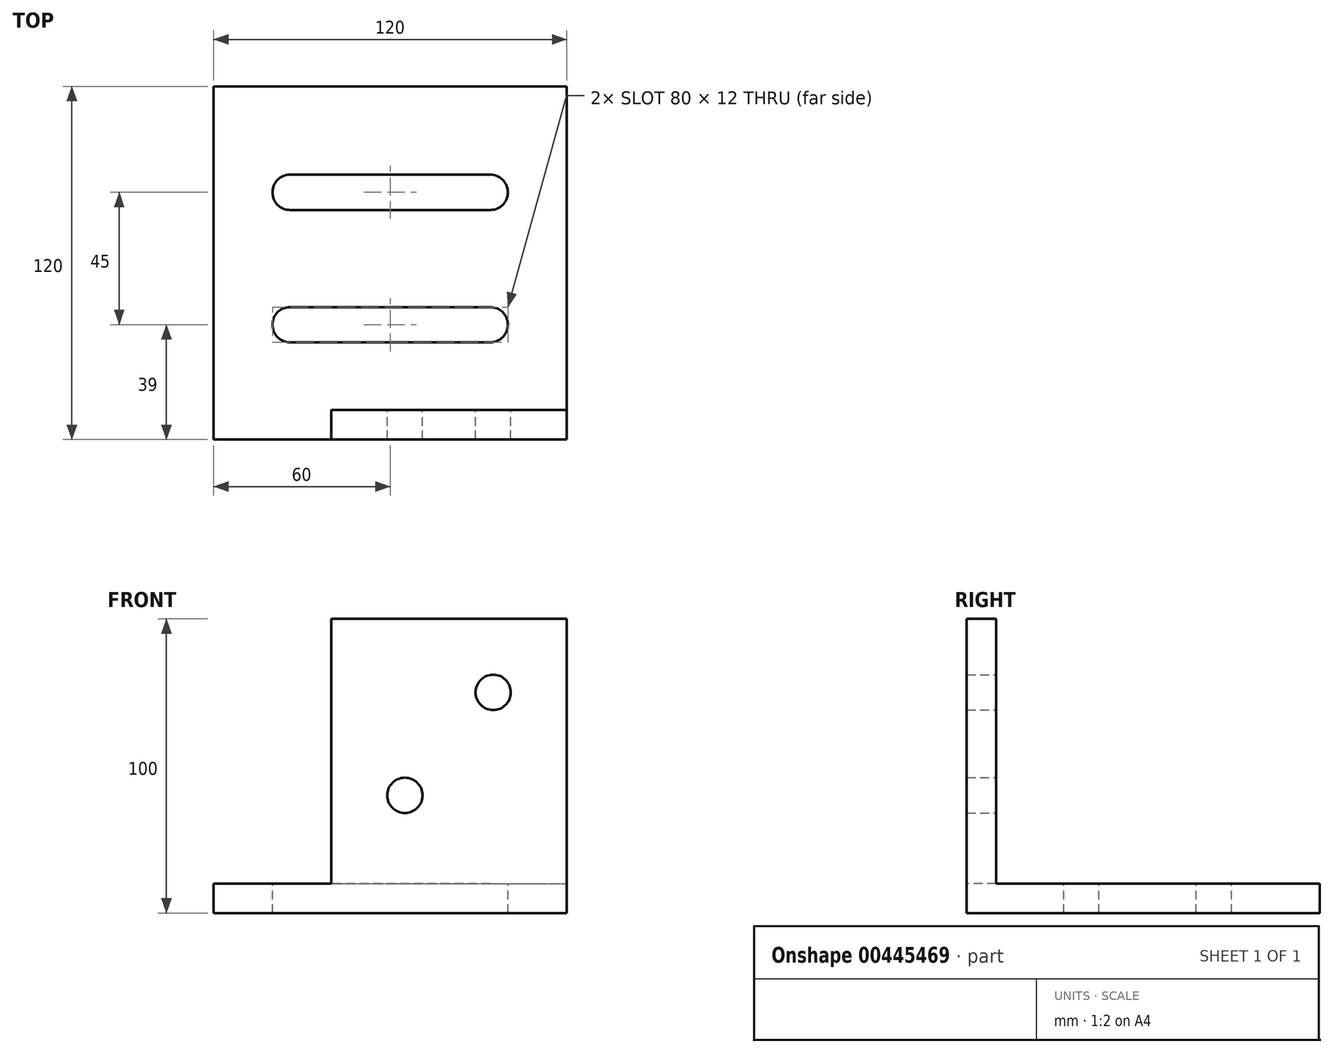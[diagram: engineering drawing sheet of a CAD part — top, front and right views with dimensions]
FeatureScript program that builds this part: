
annotation { "Feature Type Name" : "Feature", "Feature Type Description" : "" }
export const myFeature = defineFeature(function(context is Context, id is Id, definition is map)
    precondition{}
    {
        {
            var Q0;
            Q0=qCreatedBy(makeId("Front.planeOp"),FACE);
            var sketch = newSketch(context, id + "F0", { "sketchPlane" : qUnion([Q0])});
            skLineSegment(sketch, "E0.bottom", {"start": v(40, -50) * mm, "end": v(-40, -50) * mm});
            skLineSegment(sketch, "E0.top", {"start": v(40, 50) * mm, "end": v(-40, 50) * mm});
            skLineSegment(sketch, "E0.left", {"start": v(40, -50) * mm, "end": v(40, 50) * mm});
            skLineSegment(sketch, "E0.right", {"start": v(-40, -50) * mm, "end": v(-40, 50) * mm});
            skPoint(sketch, "E0.middle", {"position": v(0, 0) * mm});
            skSolve(sketch);
        }
        {
            var Q0;
            Q0 = qSketchRegion(id + "F0", true);
            extrude(context, id + "F1", {"entities" : qUnion([Q0]), "endBound" : BoundingType.SYMMETRIC, "depth" : 10 * mm, "offsetDistance" : 25 * mm});
        }
        {
            var Q0;
            Q0=makeQuery(id+"F1.opExtrude","CAP_FACE",FACE,{"disambiguationData":[OSD([sQuery(id+"F0.wireOp",EDGE,"E0.bottom"),sQuery(id+"F0.wireOp",EDGE,"E0.top"),sQuery(id+"F0.wireOp",EDGE,"E0.left"),sQuery(id+"F0.wireOp",EDGE,"E0.right")])],"isStart":false});
            var sketch = newSketch(context, id + "F2", { "sketchPlane" : qUnion([Q0])});
            skLineSegment(sketch, "E1.bottom", {"start": v(-80, -50) * mm, "end": v(40, -50) * mm});
            skLineSegment(sketch, "E1.top", {"start": v(-80, -40) * mm, "end": v(40, -40) * mm});
            skLineSegment(sketch, "E1.left", {"start": v(-80, -50) * mm, "end": v(-80, -40) * mm});
            skLineSegment(sketch, "E1.right", {"start": v(40, -50) * mm, "end": v(40, -40) * mm});
            skSolve(sketch);
        }
        {
            var Q0;
            Q0 = qSketchRegion(id + "F2", true);
            extrude(context, id + "F3", {"entities" : qUnion([Q0]), "operationType" : NewBodyOperationType.ADD, "oppositeDirection" : true, "depth" : 120 * mm, "offsetDistance" : 25 * mm});
        }
        {
            var Q0;
            Q0=makeQuery(id+"F3.opExtrude","SWEPT_FACE",FACE,{"disambiguationData":[OSD([sQuery(id+"F2.wireOp",EDGE,"E1.top")])]});
            var sketch = newSketch(context, id + "F4", { "sketchPlane" : qUnion([Q0])});
            skLineSegment(sketch, "E2.bottom", {"start": v(14, 85) * mm, "end": v(-54, 85) * mm});
            skLineSegment(sketch, "E2.top", {"start": v(14, 73) * mm, "end": v(-54, 73) * mm});
            skLineSegment(sketch, "E2.left", {"start": v(20, 79) * mm, "end": v(20, 79) * mm});
            skLineSegment(sketch, "E2.right", {"start": v(-60, 79) * mm, "end": v(-60, 79) * mm});
            skPoint(sketch, "E3.visualSharp", {"position": v(20, 85) * mm});
            skArc(sketch, "E3.filletArc", {"start": v(20, 79) * mm, "mid": v(18.24, 83.24) * mm, "end": v(14, 85) * mm});
            skPoint(sketch, "E4.visualSharp", {"position": v(20, 73) * mm});
            skArc(sketch, "E4.filletArc", {"start": v(14, 73) * mm, "mid": v(18.24, 74.76) * mm, "end": v(20, 79) * mm});
            skPoint(sketch, "E5.visualSharp", {"position": v(-60, 73) * mm});
            skArc(sketch, "E5.filletArc", {"start": v(-60, 79) * mm, "mid": v(-58.24, 74.76) * mm, "end": v(-54, 73) * mm});
            skPoint(sketch, "E6.visualSharp", {"position": v(-60, 85) * mm});
            skArc(sketch, "E6.filletArc", {"start": v(-54, 85) * mm, "mid": v(-58.24, 83.24) * mm, "end": v(-60, 79) * mm});
            skPoint(sketch, "E7.0.1.0", {"position": v(-60, 40) * mm});
            skPoint(sketch, "E7.0.1.1", {"position": v(-60, 28) * mm});
            skPoint(sketch, "E7.0.1.2", {"position": v(20, 40) * mm});
            skLineSegment(sketch, "E7.0.1.3", {"start": v(14, 28) * mm, "end": v(-54, 28) * mm});
            skPoint(sketch, "E7.0.1.4", {"position": v(20, 28) * mm});
            skLineSegment(sketch, "E7.0.1.5", {"start": v(14, 40) * mm, "end": v(-54, 40) * mm});
            skArc(sketch, "E7.0.1.6", {"start": v(20, 34) * mm, "mid": v(18.24, 38.24) * mm, "end": v(14, 40) * mm});
            skArc(sketch, "E7.0.1.7", {"start": v(-54, 40) * mm, "mid": v(-58.24, 38.24) * mm, "end": v(-60, 34) * mm});
            skArc(sketch, "E7.0.1.8", {"start": v(-60, 34) * mm, "mid": v(-58.24, 29.76) * mm, "end": v(-54, 28) * mm});
            skArc(sketch, "E7.0.1.9", {"start": v(14, 28) * mm, "mid": v(18.24, 29.76) * mm, "end": v(20, 34) * mm});
            skLineSegment(sketch, "E7.direction1", {"start": v(-60, 73) * mm, "end": v(-35, 73) * mm, "construction": true});
            skLineSegment(sketch, "E7.direction2", {"start": v(-60, 73) * mm, "end": v(-60, 28) * mm, "construction": true});
            skSolve(sketch);
        }
        {
            var Q0;
            Q0=makeQuery(id+"F4.imprint","IMPRINT",FACE,{"disambiguationData":[TD([[makeQuery(id+"F4.imprint","IMPRINT",EDGE,{"derivedFrom":sQuery(id+"F4.wireOp",EDGE,"E2.bottom")}),1.0]])]});
            var Q1;
            Q1=makeQuery(id+"F4.imprint","IMPRINT",FACE,{"disambiguationData":[TD([[makeQuery(id+"F4.imprint","IMPRINT",EDGE,{"derivedFrom":sQuery(id+"F4.wireOp",EDGE,"E7.0.1.3")}),-1.0]])]});
            extrude(context, id + "F5", {"entities" : qUnion([Q0, Q1]), "operationType" : NewBodyOperationType.REMOVE, "oppositeDirection" : true, "depth" : 25 * mm, "offsetDistance" : 25 * mm});
        }
        {
            var Q0;
            Q0=makeQuery(id+"F1.opExtrude","CAP_FACE",FACE,{"disambiguationData":[OSD([sQuery(id+"F0.wireOp",EDGE,"E0.bottom"),sQuery(id+"F0.wireOp",EDGE,"E0.top"),sQuery(id+"F0.wireOp",EDGE,"E0.left"),sQuery(id+"F0.wireOp",EDGE,"E0.right")])],"isStart":true});
            var sketch = newSketch(context, id + "F6", { "sketchPlane" : qUnion([Q0])});
            skCircle(sketch, "E8", {"center": v(-15, 25) * mm, "radius": 6 * mm});
            skCircle(sketch, "E9", {"center": v(15, -10) * mm, "radius": 6 * mm});
            skSolve(sketch);
        }
        {
            var Q0;
            Q0 = qSketchRegion(id + "F6", true);
            extrude(context, id + "F7", {"entities" : qUnion([Q0]), "operationType" : NewBodyOperationType.REMOVE, "oppositeDirection" : true, "depth" : 25 * mm, "offsetDistance" : 25 * mm});
        }
    });
